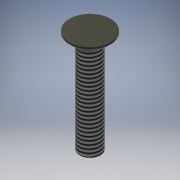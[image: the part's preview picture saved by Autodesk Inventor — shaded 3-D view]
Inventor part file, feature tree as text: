
AUTODESK INVENTOR PART (.ipt)
format: ipt  version: 2016 (Build 200138000, 138)  size: 128,000 bytes
history: native  units: mm
features: extrude x3, sketch x3, other x1, thread x1, chamfer x1
ambient origin geometry x1: Origin
bodies: Body1 (feature_tree)
feature tree (9):
  other  "ソリッド1"
  extrude  "押し出し1"  Depth=4.0mm
  extrude  "押し出し2"  Depth=6.0mm TaperAngle=0.0deg
  thread  "ねじ1"
  chamfer  "面取り1"  Distance=8.0mm
  extrude  "押し出し4"  Depth=2.3mm TaperAngle=0.0deg
  sketch  "スケッチ1"
  sketch  "スケッチ2"
  sketch  "スケッチ4"
